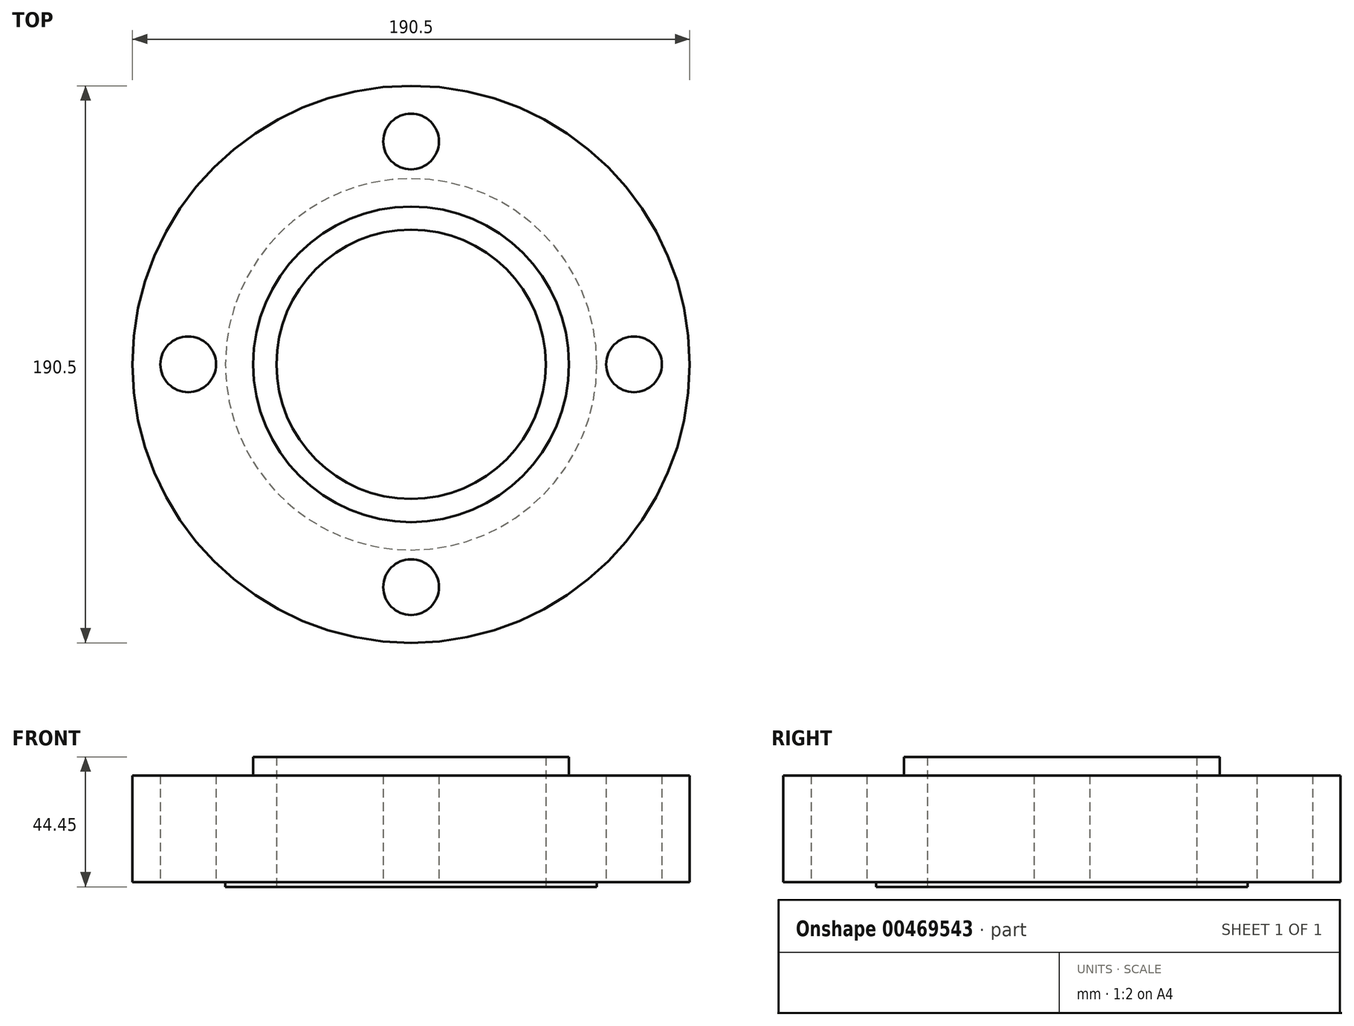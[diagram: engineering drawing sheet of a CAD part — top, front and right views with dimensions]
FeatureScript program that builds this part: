
annotation { "Feature Type Name" : "Feature", "Feature Type Description" : "" }
export const myFeature = defineFeature(function(context is Context, id is Id, definition is map)
    precondition{}
    {
        {
            var Q0;
            Q0=qCreatedBy(makeId("Front.planeOp"),FACE);
            var sketch = newSketch(context, id + "F0", { "sketchPlane" : qUnion([Q0])});
            skLineSegment(sketch, "E0", {"start": v(0, 0) * mm, "end": v(0, 44.45) * mm, "construction": true});
            skLineSegment(sketch, "E1", {"start": v(-46.04, 0) * mm, "end": v(-63.5, 0) * mm});
            skLineSegment(sketch, "E2", {"start": v(-63.5, 0) * mm, "end": v(-63.5, 1.59) * mm});
            skLineSegment(sketch, "E3", {"start": v(-63.5, 1.59) * mm, "end": v(-95.25, 1.59) * mm});
            skLineSegment(sketch, "E4", {"start": v(-95.25, 1.59) * mm, "end": v(-95.25, 38.1) * mm});
            skLineSegment(sketch, "E5", {"start": v(-95.25, 38.1) * mm, "end": v(-53.98, 38.1) * mm});
            skLineSegment(sketch, "E6", {"start": v(-53.98, 38.1) * mm, "end": v(-53.98, 44.45) * mm});
            skLineSegment(sketch, "E7", {"start": v(-53.98, 44.45) * mm, "end": v(-46.04, 44.45) * mm});
            skLineSegment(sketch, "E8", {"start": v(-46.04, 44.45) * mm, "end": v(-46.04, 0) * mm});
            skSolve(sketch);
        }
        {
            var Q0;
            Q0 = qSketchRegion(id + "F0", true);
            var Q1;
            Q1=sQuery(id+"F0.wireOp",EDGE,"E0");
            revolve(context, id + "F1", {"surfaceOperationType" : NewSurfaceOperationType.NEW, "entities" : qUnion([Q0]), "axis" : qUnion([Q1]), "revolveType" : RevolveType.FULL});
        }
        {
            var Q0;
            Q0=qCreatedBy(makeId("Top.planeOp"),FACE);
            var sketch = newSketch(context, id + "F2", { "sketchPlane" : qUnion([Q0])});
            skCircle(sketch, "E9", {"center": v(76.2, 0) * mm, "radius": 9.53 * mm});
            skCircle(sketch, "E10", {"center": v(0, 0) * mm, "radius": 76.2 * mm, "construction": true});
            skCircle(sketch, "E11", {"center": v(0, 76.2) * mm, "radius": 9.53 * mm});
            skCircle(sketch, "E12", {"center": v(-76.2, 0) * mm, "radius": 9.53 * mm});
            skCircle(sketch, "E13", {"center": v(0, -76.2) * mm, "radius": 9.53 * mm});
            skSolve(sketch);
        }
        {
            var Q0;
            Q0 = qSketchRegion(id + "F2", true);
            extrude(context, id + "F3", {"entities" : qUnion([Q0]), "operationType" : NewBodyOperationType.REMOVE, "endBound" : BoundingType.THROUGH_ALL, "depth" : 25.4 * mm, "offsetDistance" : 25.4 * mm});
        }
    });
